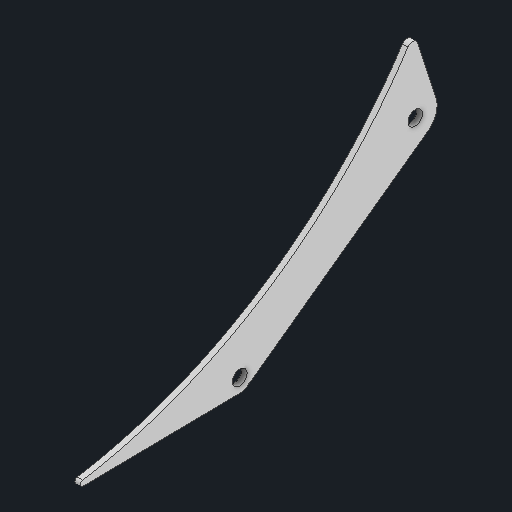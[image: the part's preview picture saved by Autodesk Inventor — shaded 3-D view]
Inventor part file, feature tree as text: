
AUTODESK INVENTOR PART (.ipt)
format: ipt  version: 2025 (Build 290162000, 162)  size: 100,864 bytes
history: native  units: in
note: dims shown in document units (in); Inventor stores cm internally (conversion verified against a paired STEP export)
features: extrude x1, sketch x1
ambient origin geometry x8: Origin, YZ Plane, XZ Plane, XY Plane, X Axis, Y Axis, Z Axis, Center Point
bodies: Solid1 (feature_tree)
feature tree (2):
  extrude  "Extrusion1"  Depth=0.0625in TaperAngle=0.0deg
  sketch  "Sketch1"  dims[d1=0.5in d3=0.0625in d4=0.0in d5=0.164in d6=0.0312in d7=5.5in]
